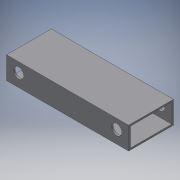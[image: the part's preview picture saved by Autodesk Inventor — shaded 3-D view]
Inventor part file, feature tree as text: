
AUTODESK INVENTOR PART (.ipt)
format: ipt  version: 2018 (Build 220112000, 112)  size: 117,760 bytes
history: native  units: mm
features: other x4, sketch x3, hole x2, extrude x1, reference x1
ambient origin geometry x8: Origin, YZ Plane, XZ Plane, XY Plane, X Axis, Y Axis, Z Axis, Center Point
bodies: Body1 (feature_tree)
feature tree (11):
  other  "ソリッド1"
  extrude  "押し出し1"  Depth=60.0mm
  hole  "穴1"  [1 undecoded]
  hole  "穴2"  [1 undecoded]
  sketch  "スケッチ1"
  sketch  "スケッチ2"
  sketch  "スケッチ5"
  reference  "参照3"
  other  "<userpath>\Documents\RBBR\CAD\カート.iam"
  other  "カート.iam"
  other  "後輪:1"
note: 2 required parameter values undecoded (feature->parameter linkage not recoverable at this tier; creation-order binding heuristic only, values carry confidence <= 0.55)
